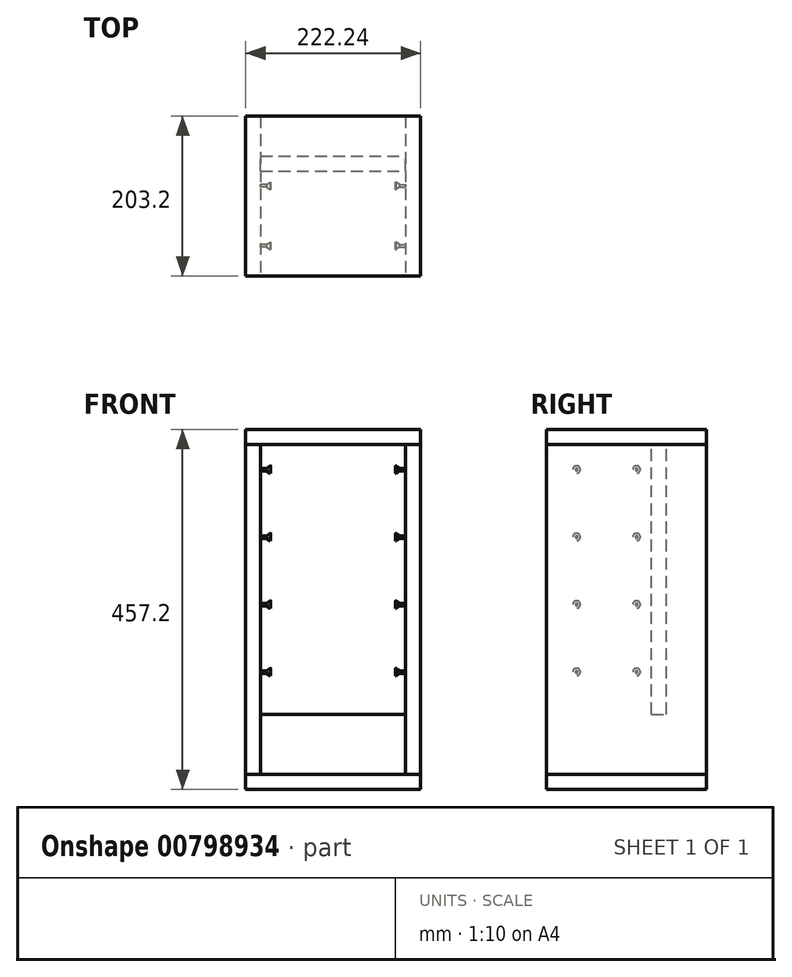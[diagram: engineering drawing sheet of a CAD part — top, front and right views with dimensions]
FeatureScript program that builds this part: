
annotation { "Feature Type Name" : "Feature", "Feature Type Description" : "" }
export const myFeature = defineFeature(function(context is Context, id is Id, definition is map)
    precondition{}
    {
        {
            var Q0;
            Q0=qCreatedBy(makeId("Top.planeOp"),FACE);
            var sketch = newSketch(context, id + "F0", { "sketchPlane" : qUnion([Q0])});
            skLineSegment(sketch, "E0.bottom", {"start": v(111.13, -101.6) * mm, "end": v(-111.13, -101.6) * mm});
            skLineSegment(sketch, "E0.top", {"start": v(111.13, 101.6) * mm, "end": v(-111.12, 101.6) * mm});
            skLineSegment(sketch, "E0.left", {"start": v(111.13, -101.6) * mm, "end": v(111.13, 101.6) * mm});
            skLineSegment(sketch, "E0.right", {"start": v(-111.13, -101.6) * mm, "end": v(-111.12, 101.6) * mm});
            skPoint(sketch, "E0.middle", {"position": v(0, 0) * mm});
            skSolve(sketch);
        }
        {
            var Q0;
            Q0 = qSketchRegion(id + "F0", true);
            extrude(context, id + "F1", {"entities" : qUnion([Q0]), "depth" : 19.05 * mm, "offsetDistance" : 25.4 * mm});
        }
        {
            var Q0;
            Q0=makeQuery(id+"F1.opExtrude","CAP_FACE",FACE,{"disambiguationData":[OSD([sQuery(id+"F0.wireOp",EDGE,"E0.bottom"),sQuery(id+"F0.wireOp",EDGE,"E0.top"),sQuery(id+"F0.wireOp",EDGE,"E0.left"),sQuery(id+"F0.wireOp",EDGE,"E0.right")])],"isStart":false});
            var sketch = newSketch(context, id + "F2", { "sketchPlane" : qUnion([Q0])});
            skLineSegment(sketch, "E1", {"start": v(-111.12, 101.6) * mm, "end": v(-92.08, 101.6) * mm});
            skLineSegment(sketch, "E2", {"start": v(-92.08, 101.6) * mm, "end": v(-92.07, -101.6) * mm});
            skLineSegment(sketch, "E3", {"start": v(-92.07, -101.6) * mm, "end": v(-111.13, -101.6) * mm});
            skLineSegment(sketch, "E4", {"start": v(-111.12, -101.6) * mm, "end": v(-111.12, 101.6) * mm});
            skLineSegment(sketch, "E5.MirrorCS", {"start": v(92.08, 101.6) * mm, "end": v(92.07, -101.6) * mm});
            skLineSegment(sketch, "E6.MirrorCS", {"start": v(111.12, 101.6) * mm, "end": v(92.08, 101.6) * mm});
            skLineSegment(sketch, "E7.MirrorCS", {"start": v(111.12, -101.6) * mm, "end": v(111.12, 101.6) * mm});
            skLineSegment(sketch, "E8.MirrorCS", {"start": v(92.07, -101.6) * mm, "end": v(111.13, -101.6) * mm});
            skSolve(sketch);
        }
        {
            var Q0;
            Q0 = qSketchRegion(id + "F2", true);
            extrude(context, id + "F3", {"entities" : qUnion([Q0]), "depth" : 419.1 * mm, "offsetDistance" : 25.4 * mm});
        }
        {
            var Q0;
            Q0=makeQuery(id+"F3.opExtrude","CAP_FACE",FACE,{"disambiguationData":[OSD([sQuery(id+"F2.wireOp",EDGE,"E1"),sQuery(id+"F2.wireOp",EDGE,"E2"),sQuery(id+"F2.wireOp",EDGE,"E3"),sQuery(id+"F2.wireOp",EDGE,"E4")])],"isStart":false});
            var sketch = newSketch(context, id + "F4", { "sketchPlane" : qUnion([Q0])});
            skLineSegment(sketch, "E9.0.0", {"start": v(111.13, -101.6) * mm, "end": v(111.13, 101.6) * mm});
            skLineSegment(sketch, "E9.0.1", {"start": v(111.13, 101.6) * mm, "end": v(-111.12, 101.6) * mm});
            skLineSegment(sketch, "E9.0.2", {"start": v(-111.12, 101.6) * mm, "end": v(-111.12, -101.6) * mm});
            skLineSegment(sketch, "E9.0.3", {"start": v(-111.13, -101.6) * mm, "end": v(111.13, -101.6) * mm});
            skSolve(sketch);
        }
        {
            var Q0;
            Q0 = qSketchRegion(id + "F4", true);
            extrude(context, id + "F5", {"entities" : qUnion([Q0]), "depth" : 19.05 * mm, "offsetDistance" : 25.4 * mm});
        }
        {
            var Q0;
            Q0=makeQuery(id+"F5.opExtrude","CAP_FACE",FACE,{"disambiguationData":[OSD([sQuery(id+"F4.wireOp",EDGE,"E9.0.0"),sQuery(id+"F4.wireOp",EDGE,"E9.0.1"),sQuery(id+"F4.wireOp",EDGE,"E9.0.2"),sQuery(id+"F4.wireOp",EDGE,"E9.0.3")])],"isStart":true});
            var sketch = newSketch(context, id + "F6", { "sketchPlane" : qUnion([Q0])});
            skLineSegment(sketch, "E10.0", {"start": v(-92.08, -101.6) * mm, "end": v(-92.07, 101.6) * mm, "construction": true});
            skLineSegment(sketch, "E11.0", {"start": v(92.08, -101.6) * mm, "end": v(92.07, 101.6) * mm, "construction": true});
            skLineSegment(sketch, "E12.bottom", {"start": v(-92.07, -31.75) * mm, "end": v(92.07, -31.75) * mm});
            skLineSegment(sketch, "E12.top", {"start": v(-92.07, -50.8) * mm, "end": v(92.08, -50.8) * mm});
            skLineSegment(sketch, "E12.left", {"start": v(-92.07, -31.75) * mm, "end": v(-92.07, -50.8) * mm});
            skLineSegment(sketch, "E12.right", {"start": v(92.07, -31.75) * mm, "end": v(92.07, -50.8) * mm});
            skSolve(sketch);
        }
        {
            var Q0;
            Q0 = qSketchRegion(id + "F6", true);
            extrude(context, id + "F7", {"entities" : qUnion([Q0]), "depth" : 342.9 * mm, "offsetDistance" : 25.4 * mm});
        }
        {
            var Q0;
            Q0=makeQuery(id+"F3.opExtrude","SWEPT_FACE",FACE,{"disambiguationData":[OSD([sQuery(id+"F2.wireOp",EDGE,"E5.MirrorCS")])]});
            var sketch = newSketch(context, id + "F8", { "sketchPlane" : qUnion([Q0])});
            skLineSegment(sketch, "E13", {"start": v(63.5, 438.15) * mm, "end": v(63.5, 19.05) * mm, "construction": true});
            skLineSegment(sketch, "E14", {"start": v(-12.7, 438.15) * mm, "end": v(-12.7, 19.05) * mm, "construction": true});
            skCircle(sketch, "E15", {"center": v(-12.7, 406.4) * mm, "radius": 1.59 * mm});
            skLineSegment(sketch, "E16.direction1", {"start": v(-12.7, 406.4) * mm, "end": v(63.5, 406.4) * mm, "construction": true});
            skLineSegment(sketch, "E16.direction2", {"start": v(-12.7, 406.4) * mm, "end": v(-12.7, 320.68) * mm, "construction": true});
            skCircle(sketch, "E17", {"center": v(-12.7, 406.4) * mm, "radius": 4.76 * mm});
            skCircle(sketch, "E18.0.1.0", {"center": v(-12.7, 320.68) * mm, "radius": 1.59 * mm});
            skCircle(sketch, "E18.0.1.1", {"center": v(-12.7, 320.68) * mm, "radius": 4.76 * mm});
            skCircle(sketch, "E18.0.2.0", {"center": v(-12.7, 234.95) * mm, "radius": 1.59 * mm});
            skCircle(sketch, "E18.0.2.1", {"center": v(-12.7, 234.95) * mm, "radius": 4.76 * mm});
            skCircle(sketch, "E18.0.3.0", {"center": v(-12.7, 149.23) * mm, "radius": 1.59 * mm});
            skCircle(sketch, "E18.0.3.1", {"center": v(-12.7, 149.23) * mm, "radius": 4.76 * mm});
            skCircle(sketch, "E18.1.0.0", {"center": v(63.5, 406.4) * mm, "radius": 1.59 * mm});
            skCircle(sketch, "E18.1.0.1", {"center": v(63.5, 406.4) * mm, "radius": 4.76 * mm});
            skCircle(sketch, "E18.1.1.0", {"center": v(63.5, 320.68) * mm, "radius": 1.59 * mm});
            skCircle(sketch, "E18.1.1.1", {"center": v(63.5, 320.68) * mm, "radius": 4.76 * mm});
            skCircle(sketch, "E18.1.2.0", {"center": v(63.5, 234.95) * mm, "radius": 1.59 * mm});
            skCircle(sketch, "E18.1.2.1", {"center": v(63.5, 234.95) * mm, "radius": 4.76 * mm});
            skCircle(sketch, "E18.1.3.0", {"center": v(63.5, 149.23) * mm, "radius": 1.59 * mm});
            skCircle(sketch, "E18.1.3.1", {"center": v(63.5, 149.23) * mm, "radius": 4.76 * mm});
            skSolve(sketch);
        }
        {
            var Q0;
            Q0=makeQuery(id+"F8.imprint","IMPRINT",FACE,{"disambiguationData":[TD([[makeQuery(id+"F8.imprint","IMPRINT",EDGE,{"derivedFrom":sQuery(id+"F8.wireOp",EDGE,"E15")}),1.0]])]});
            var Q1;
            Q1=makeQuery(id+"F8.imprint","IMPRINT",FACE,{"disambiguationData":[TD([[makeQuery(id+"F8.imprint","IMPRINT",EDGE,{"derivedFrom":sQuery(id+"F8.wireOp",EDGE,"E18.1.0.0")}),1.0]])]});
            var Q2;
            Q2=makeQuery(id+"F8.imprint","IMPRINT",FACE,{"disambiguationData":[TD([[makeQuery(id+"F8.imprint","IMPRINT",EDGE,{"derivedFrom":sQuery(id+"F8.wireOp",EDGE,"E18.0.1.0")}),1.0]])]});
            var Q3;
            Q3=makeQuery(id+"F8.imprint","IMPRINT",FACE,{"disambiguationData":[TD([[makeQuery(id+"F8.imprint","IMPRINT",EDGE,{"derivedFrom":sQuery(id+"F8.wireOp",EDGE,"E18.1.1.0")}),1.0]])]});
            var Q4;
            Q4=makeQuery(id+"F8.imprint","IMPRINT",FACE,{"disambiguationData":[TD([[makeQuery(id+"F8.imprint","IMPRINT",EDGE,{"derivedFrom":sQuery(id+"F8.wireOp",EDGE,"E18.0.2.0")}),1.0]])]});
            var Q5;
            Q5=makeQuery(id+"F8.imprint","IMPRINT",FACE,{"disambiguationData":[TD([[makeQuery(id+"F8.imprint","IMPRINT",EDGE,{"derivedFrom":sQuery(id+"F8.wireOp",EDGE,"E18.1.2.0")}),1.0]])]});
            var Q6;
            Q6=makeQuery(id+"F8.imprint","IMPRINT",FACE,{"disambiguationData":[TD([[makeQuery(id+"F8.imprint","IMPRINT",EDGE,{"derivedFrom":sQuery(id+"F8.wireOp",EDGE,"E18.0.3.0")}),1.0]])]});
            var Q7;
            Q7=makeQuery(id+"F8.imprint","IMPRINT",FACE,{"disambiguationData":[TD([[makeQuery(id+"F8.imprint","IMPRINT",EDGE,{"derivedFrom":sQuery(id+"F8.wireOp",EDGE,"E18.1.3.0")}),1.0]])]});
            extrude(context, id + "F9", {"entities" : qUnion([Q0, Q1, Q2, Q3, Q4, Q5, Q6, Q7]), "operationType" : NewBodyOperationType.ADD, "depth" : 7.62 * mm, "offsetDistance" : 25.4 * mm});
        }
        {
            var Q0;
            Q0=makeQuery(id+"F9.opExtrude","CAP_FACE",FACE,{"disambiguationData":[OSD([sQuery(id+"F8.wireOp",EDGE,"E15")])],"isStart":false});
            var sketch = newSketch(context, id + "F10", { "sketchPlane" : qUnion([Q0])});
            skCircle(sketch, "E19.0", {"center": v(-12.7, 406.4) * mm, "radius": 4.76 * mm});
            skCircle(sketch, "E20.0", {"center": v(63.5, 406.4) * mm, "radius": 4.76 * mm});
            skCircle(sketch, "E21.0", {"center": v(63.5, 320.68) * mm, "radius": 4.76 * mm});
            skCircle(sketch, "E22.0", {"center": v(-12.7, 320.68) * mm, "radius": 4.76 * mm});
            skCircle(sketch, "E23.0", {"center": v(-12.7, 234.95) * mm, "radius": 4.76 * mm});
            skCircle(sketch, "E24.0", {"center": v(63.5, 234.95) * mm, "radius": 4.76 * mm});
            skCircle(sketch, "E25.0", {"center": v(-12.7, 149.23) * mm, "radius": 4.76 * mm});
            skCircle(sketch, "E26.0", {"center": v(63.5, 149.23) * mm, "radius": 4.76 * mm});
            skSolve(sketch);
        }
        {
            var Q0;
            Q0 = qSketchRegion(id + "F10", true);
            extrude(context, id + "F11", {"entities" : qUnion([Q0]), "operationType" : NewBodyOperationType.ADD, "depth" : 5.08 * mm, "offsetDistance" : 25.4 * mm, "hasSecondDirection" : true, "secondDirectionOppositeDirection" : false, "secondDirectionDepth" : 4.83 * mm});
        }
        {
            var Q1;
            Q1=makeQuery(id+"F11.opExtrude","CAP_FACE",FACE,{"disambiguationData":[OSD([sQuery(id+"F10.wireOp",EDGE,"E20.0")])],"isStart":true});
            var Q2;
            Q2=makeQuery(id+"F9.opExtrude","CAP_FACE",FACE,{"disambiguationData":[OSD([sQuery(id+"F8.wireOp",EDGE,"E18.1.0.0")])],"isStart":false});
            loft(context, id + "F12", {"operationType" : NewBodyOperationType.ADD, "sheetProfilesArray" : [{ "sheetProfileEntities" : qUnion([Q1]) }, { "sheetProfileEntities" : qUnion([Q2]) }]});
        }
        {
            var Q1;
            Q1=makeQuery(id+"F11.opExtrude","CAP_FACE",FACE,{"disambiguationData":[OSD([sQuery(id+"F10.wireOp",EDGE,"E19.0")])],"isStart":true});
            var Q2;
            Q2=makeQuery(id+"F9.opExtrude","CAP_FACE",FACE,{"disambiguationData":[OSD([sQuery(id+"F8.wireOp",EDGE,"E15")])],"isStart":false});
            loft(context, id + "F13", {"operationType" : NewBodyOperationType.ADD, "sheetProfilesArray" : [{ "sheetProfileEntities" : qUnion([Q1]) }, { "sheetProfileEntities" : qUnion([Q2]) }]});
        }
        {
            var Q0;
            Q0=makeQuery(id+"F11.opExtrude","CAP_FACE",FACE,{"disambiguationData":[OSD([sQuery(id+"F10.wireOp",EDGE,"E21.0")])],"isStart":true});
            var Q1;
            Q1=makeQuery(id+"F9.opExtrude","CAP_FACE",FACE,{"disambiguationData":[OSD([sQuery(id+"F8.wireOp",EDGE,"E18.1.1.0")])],"isStart":false});
            loft(context, id + "F14", {"operationType" : NewBodyOperationType.ADD, "sheetProfilesArray" : [{ "sheetProfileEntities" : qUnion([Q0]) }, { "sheetProfileEntities" : qUnion([Q1]) }]});
        }
        {
            var Q0;
            Q0=makeQuery(id+"F9.opExtrude","CAP_FACE",FACE,{"disambiguationData":[OSD([sQuery(id+"F8.wireOp",EDGE,"E18.0.1.0")])],"isStart":false});
            var Q1;
            Q1=makeQuery(id+"F11.opExtrude","CAP_FACE",FACE,{"disambiguationData":[OSD([sQuery(id+"F10.wireOp",EDGE,"E22.0")])],"isStart":true});
            loft(context, id + "F15", {"operationType" : NewBodyOperationType.ADD, "sheetProfilesArray" : [{ "sheetProfileEntities" : qUnion([Q0]) }, { "sheetProfileEntities" : qUnion([Q1]) }]});
        }
        {
            var Q0;
            Q0=makeQuery(id+"F9.opExtrude","CAP_FACE",FACE,{"disambiguationData":[OSD([sQuery(id+"F8.wireOp",EDGE,"E18.1.2.0")])],"isStart":false});
            var Q1;
            Q1=makeQuery(id+"F11.opExtrude","CAP_FACE",FACE,{"disambiguationData":[OSD([sQuery(id+"F10.wireOp",EDGE,"E24.0")])],"isStart":true});
            loft(context, id + "F16", {"operationType" : NewBodyOperationType.ADD, "sheetProfilesArray" : [{ "sheetProfileEntities" : qUnion([Q0]) }, { "sheetProfileEntities" : qUnion([Q1]) }]});
        }
        {
            var Q0;
            Q0=makeQuery(id+"F11.opExtrude","CAP_FACE",FACE,{"disambiguationData":[OSD([sQuery(id+"F10.wireOp",EDGE,"E23.0")])],"isStart":true});
            var Q1;
            Q1=makeQuery(id+"F9.opExtrude","CAP_FACE",FACE,{"disambiguationData":[OSD([sQuery(id+"F8.wireOp",EDGE,"E18.0.2.0")])],"isStart":false});
            loft(context, id + "F17", {"operationType" : NewBodyOperationType.ADD, "sheetProfilesArray" : [{ "sheetProfileEntities" : qUnion([Q0]) }, { "sheetProfileEntities" : qUnion([Q1]) }]});
        }
        {
            var Q0;
            Q0=makeQuery(id+"F9.opExtrude","CAP_FACE",FACE,{"disambiguationData":[OSD([sQuery(id+"F8.wireOp",EDGE,"E18.0.3.0")])],"isStart":false});
            var Q1;
            Q1=makeQuery(id+"F11.opExtrude","CAP_FACE",FACE,{"disambiguationData":[OSD([sQuery(id+"F10.wireOp",EDGE,"E25.0")])],"isStart":true});
            loft(context, id + "F18", {"operationType" : NewBodyOperationType.ADD, "sheetProfilesArray" : [{ "sheetProfileEntities" : qUnion([Q0]) }, { "sheetProfileEntities" : qUnion([Q1]) }]});
        }
        {
            var Q0;
            Q0=makeQuery(id+"F9.opExtrude","CAP_FACE",FACE,{"disambiguationData":[OSD([sQuery(id+"F8.wireOp",EDGE,"E18.1.3.0")])],"isStart":false});
            var Q1;
            Q1=makeQuery(id+"F11.opExtrude","CAP_FACE",FACE,{"disambiguationData":[OSD([sQuery(id+"F10.wireOp",EDGE,"E26.0")])],"isStart":true});
            loft(context, id + "F19", {"operationType" : NewBodyOperationType.ADD, "sheetProfilesArray" : [{ "sheetProfileEntities" : qUnion([Q0]) }, { "sheetProfileEntities" : qUnion([Q1]) }]});
        }
        {
            var Q0;
            Q0=makeQuery(id+"F3.opExtrude","SWEPT_BODY",BODY,{"disambiguationData":[OSD([sQuery(id+"F2.wireOp",EDGE,"E5.MirrorCS"),sQuery(id+"F2.wireOp",EDGE,"E6.MirrorCS"),sQuery(id+"F2.wireOp",EDGE,"E7.MirrorCS"),sQuery(id+"F2.wireOp",EDGE,"E8.MirrorCS")])]});
            var Q1;
            Q1=qCreatedBy(makeId("Right.planeOp"),FACE);
            mirror(context, id + "F20", {"entities" : qUnion([Q0]), "mirrorPlane" : qUnion([Q1])});
        }
        {
            var Q0;
            Q0=makeQuery(id+"F3.opExtrude","SWEPT_BODY",BODY,{"disambiguationData":[OSD([sQuery(id+"F2.wireOp",EDGE,"E1"),sQuery(id+"F2.wireOp",EDGE,"E2"),sQuery(id+"F2.wireOp",EDGE,"E3"),sQuery(id+"F2.wireOp",EDGE,"E4")])]});
            deleteBodies(context, id + "F21", {"entities" : qUnion([Q0])});
        }
    });
